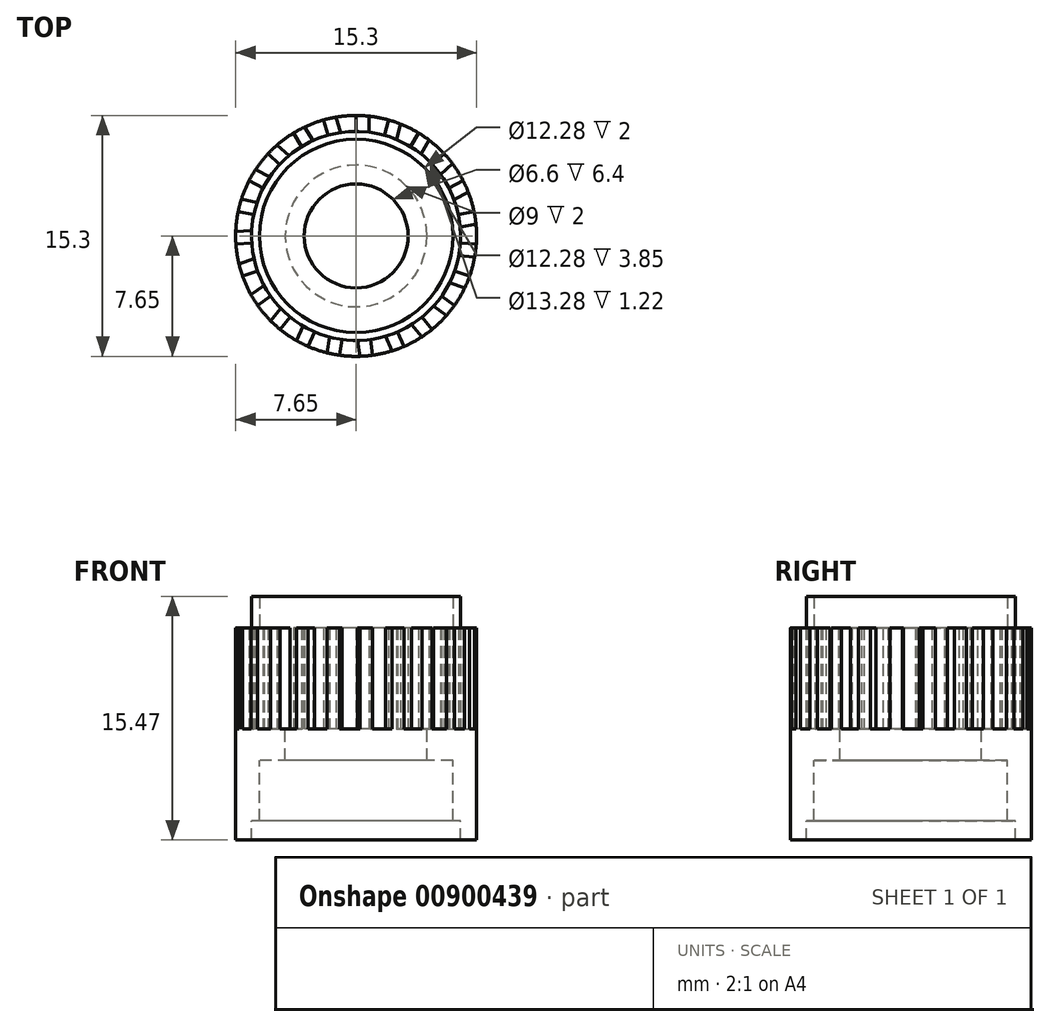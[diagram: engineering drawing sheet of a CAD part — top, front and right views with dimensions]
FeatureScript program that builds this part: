
annotation { "Feature Type Name" : "Feature", "Feature Type Description" : "" }
export const myFeature = defineFeature(function(context is Context, id is Id, definition is map)
    precondition{}
    {
        {
            var Q0;
            Q0=qCreatedBy(makeId("Top.planeOp"),FACE);
            var sketch = newSketch(context, id + "F0", { "sketchPlane" : qUnion([Q0])});
            skCircle(sketch, "E0", {"center": v(0, 0.97) * mm, "radius": 6.14 * mm});
            skCircle(sketch, "E1", {"center": v(0, 0.97) * mm, "radius": 7.65 * mm});
            skLineSegment(sketch, "E2", {"start": v(0, 7.11) * mm, "end": v(0, 8.62) * mm});
            skLineSegment(sketch, "E3", {"start": v(0.8, 7.06) * mm, "end": v(0.8, 8.58) * mm});
            skCircle(sketch, "E4", {"center": v(0, 0.97) * mm, "radius": 3.3 * mm});
            skCircle(sketch, "E5", {"center": v(0, 0.97) * mm, "radius": 4.5 * mm});
            skCircle(sketch, "E6", {"center": v(0, 0.97) * mm, "radius": 6.64 * mm});
            skCircle(sketch, "E7", {"center": v(0, 0.97) * mm, "radius": 7.45 * mm});
            skCircle(sketch, "E8", {"center": v(0, 0.97) * mm, "radius": 9 * mm});
            skCircle(sketch, "E9", {"center": v(0, 0.97) * mm, "radius": 10 * mm});
            skSolve(sketch);
        }
        {
            var Q0;
            Q0=makeQuery(id+"F0.imprint","IMPRINT",FACE,{"disambiguationData":[TD([[makeQuery(id+"F0.imprint","IMPRINT",EDGE,{"derivedFrom":sQuery(id+"F0.wireOp",EDGE,"E4")}),-1.0]])]});
            var Q1;
            Q1=makeQuery(id+"F0.imprint","IMPRINT",FACE,{"disambiguationData":[TD([[makeQuery(id+"F0.imprint","IMPRINT",EDGE,{"derivedFrom":sQuery(id+"F0.wireOp",EDGE,"E5")}),-1.0]])]});
            var Q2;
            {var subQ0=sQuery(id+"F0.wireOp",EDGE,"E2");var subQ1=sQuery(id+"F0.wireOp",EDGE,"E0");var subQ2=makeQuery(id+"F0.imprint","INTERSECT",VERTEX,{"derivedFrom":[subQ1,subQ0]});Q2=makeQuery(id+"F0.imprint","IMPRINT",FACE,{"disambiguationData":[TD([[makeQuery(id+"F0.imprint","IMPRINT",EDGE,{"disambiguationData":[TD([[subQ2,1.0]])],"derivedFrom":subQ1}),-1.0]])]});}
            var Q3;
            {var subQ0=sQuery(id+"F0.wireOp",EDGE,"E6");var subQ1=sQuery(id+"F0.wireOp",EDGE,"E2");var subQ2=makeQuery(id+"F0.imprint","INTERSECT",VERTEX,{"derivedFrom":[subQ1,subQ0]});Q3=makeQuery(id+"F0.imprint","IMPRINT",FACE,{"disambiguationData":[TD([[makeQuery(id+"F0.imprint","IMPRINT",EDGE,{"disambiguationData":[TD([[subQ2,-1.0]])],"derivedFrom":subQ1}),-1.0]])]});}
            var Q4;
            {var subQ0=sQuery(id+"F0.wireOp",EDGE,"E2");var subQ1=sQuery(id+"F0.wireOp",EDGE,"E1");var subQ2=makeQuery(id+"F0.imprint","INTERSECT",VERTEX,{"derivedFrom":[subQ1,subQ0]});Q4=makeQuery(id+"F0.imprint","IMPRINT",FACE,{"disambiguationData":[TD([[makeQuery(id+"F0.imprint","IMPRINT",EDGE,{"disambiguationData":[TD([[subQ2,1.0]])],"derivedFrom":subQ1}),1.0]])]});}
            extrude(context, id + "F1", {"entities" : qUnion([Q0, Q1, Q2, Q3, Q4]), "depth" : 6.4 * mm, "offsetDistance" : 25 * mm});
        }
        {
            var Q0;
            {var subQ0=sQuery(id+"F0.wireOp",EDGE,"E2");var subQ1=sQuery(id+"F0.wireOp",EDGE,"E0");var subQ2=makeQuery(id+"F0.imprint","INTERSECT",VERTEX,{"derivedFrom":[subQ1,subQ0]});Q0=makeQuery(id+"F0.imprint","IMPRINT",FACE,{"disambiguationData":[TD([[makeQuery(id+"F0.imprint","IMPRINT",EDGE,{"disambiguationData":[TD([[subQ2,-1.0]])],"derivedFrom":subQ1}),-1.0]])]});}
            var Q1;
            {var subQ0=sQuery(id+"F0.wireOp",EDGE,"E2");var subQ1=sQuery(id+"F0.wireOp",EDGE,"E0");var subQ2=makeQuery(id+"F0.imprint","INTERSECT",VERTEX,{"derivedFrom":[subQ1,subQ0]});Q1=makeQuery(id+"F0.imprint","IMPRINT",FACE,{"disambiguationData":[TD([[makeQuery(id+"F0.imprint","IMPRINT",EDGE,{"disambiguationData":[TD([[subQ2,1.0]])],"derivedFrom":subQ1}),-1.0]])]});}
            extrude(context, id + "F2", {"entities" : qUnion([Q0, Q1]), "depth" : 8.4 * mm, "offsetDistance" : 25 * mm});
        }
        {
            var Q0;
            Q0=qCreatedBy(makeId("Right.planeOp"),FACE);
            var sketch = newSketch(context, id + "F3", { "sketchPlane" : qUnion([Q0])});
            skLineSegment(sketch, "E10", {"start": v(0.97, 0) * mm, "end": v(0.97, -2.16) * mm});
            skSolve(sketch);
        }
        {
            var Q0;
            Q0=makeQuery(id+"F1.opExtrude","SWEPT_BODY",BODY,{"disambiguationData":[OSD([sQuery(id+"F0.wireOp",EDGE,"E0"),sQuery(id+"F0.wireOp",EDGE,"E1"),sQuery(id+"F0.wireOp",EDGE,"E2"),sQuery(id+"F0.wireOp",EDGE,"E3"),sQuery(id+"F0.wireOp",EDGE,"E4")])]});
            var Q1;
            Q1=sQuery(id+"F3.wireOp",EDGE,"E10");
            circularPattern(context, id + "F4", {"operationType" : NewBodyOperationType.ADD, "entities" : qUnion([Q0]), "axis" : qUnion([Q1]), "angle" : 360 * degree, "instanceCount" : 23, "equalSpace" : true});
        }
        {
            var Q0;
            Q0=makeQuery(id+"F0.imprint","IMPRINT",FACE,{"disambiguationData":[TD([[makeQuery(id+"F0.imprint","IMPRINT",EDGE,{"derivedFrom":sQuery(id+"F0.wireOp",EDGE,"E5")}),-1.0]])]});
            extrude(context, id + "F5", {"entities" : qUnion([Q0]), "operationType" : NewBodyOperationType.ADD, "oppositeDirection" : true, "depth" : 2 * mm, "offsetDistance" : 25 * mm});
        }
        {
            var Q0;
            {var subQ0=sQuery(id+"F0.wireOp",EDGE,"E2");var subQ1=sQuery(id+"F0.wireOp",EDGE,"E0");var subQ2=makeQuery(id+"F0.imprint","INTERSECT",VERTEX,{"derivedFrom":[subQ1,subQ0]});Q0=makeQuery(id+"F0.imprint","IMPRINT",FACE,{"disambiguationData":[TD([[makeQuery(id+"F0.imprint","IMPRINT",EDGE,{"disambiguationData":[TD([[subQ2,-1.0]])],"derivedFrom":subQ1}),-1.0]])]});}
            var Q1;
            {var subQ0=sQuery(id+"F0.wireOp",EDGE,"E2");var subQ1=sQuery(id+"F0.wireOp",EDGE,"E0");var subQ2=makeQuery(id+"F0.imprint","INTERSECT",VERTEX,{"derivedFrom":[subQ1,subQ0]});Q1=makeQuery(id+"F0.imprint","IMPRINT",FACE,{"disambiguationData":[TD([[makeQuery(id+"F0.imprint","IMPRINT",EDGE,{"disambiguationData":[TD([[subQ2,1.0]])],"derivedFrom":subQ1}),-1.0]])]});}
            extrude(context, id + "F6", {"entities" : qUnion([Q0, Q1]), "operationType" : NewBodyOperationType.ADD, "oppositeDirection" : true, "depth" : 5.85 * mm, "offsetDistance" : 25 * mm});
        }
        {
            var Q0;
            {var subQ0=sQuery(id+"F0.wireOp",EDGE,"E6");var subQ1=sQuery(id+"F0.wireOp",EDGE,"E2");var subQ2=makeQuery(id+"F0.imprint","INTERSECT",VERTEX,{"derivedFrom":[subQ1,subQ0]});Q0=makeQuery(id+"F0.imprint","IMPRINT",FACE,{"disambiguationData":[TD([[makeQuery(id+"F0.imprint","IMPRINT",EDGE,{"disambiguationData":[TD([[subQ2,-1.0]])],"derivedFrom":subQ1}),1.0]])]});}
            var Q1;
            {var subQ0=sQuery(id+"F0.wireOp",EDGE,"E2");var subQ1=sQuery(id+"F0.wireOp",EDGE,"E1");var subQ2=makeQuery(id+"F0.imprint","INTERSECT",VERTEX,{"derivedFrom":[subQ1,subQ0]});Q1=makeQuery(id+"F0.imprint","IMPRINT",FACE,{"disambiguationData":[TD([[makeQuery(id+"F0.imprint","IMPRINT",EDGE,{"disambiguationData":[TD([[subQ2,-1.0]])],"derivedFrom":subQ1}),1.0]])]});}
            var Q2;
            {var subQ0=sQuery(id+"F0.wireOp",EDGE,"E6");var subQ1=sQuery(id+"F0.wireOp",EDGE,"E2");var subQ2=makeQuery(id+"F0.imprint","INTERSECT",VERTEX,{"derivedFrom":[subQ1,subQ0]});Q2=makeQuery(id+"F0.imprint","IMPRINT",FACE,{"disambiguationData":[TD([[makeQuery(id+"F0.imprint","IMPRINT",EDGE,{"disambiguationData":[TD([[subQ2,-1.0]])],"derivedFrom":subQ1}),-1.0]])]});}
            var Q3;
            {var subQ0=sQuery(id+"F0.wireOp",EDGE,"E2");var subQ1=sQuery(id+"F0.wireOp",EDGE,"E1");var subQ2=makeQuery(id+"F0.imprint","INTERSECT",VERTEX,{"derivedFrom":[subQ1,subQ0]});Q3=makeQuery(id+"F0.imprint","IMPRINT",FACE,{"disambiguationData":[TD([[makeQuery(id+"F0.imprint","IMPRINT",EDGE,{"disambiguationData":[TD([[subQ2,1.0]])],"derivedFrom":subQ1}),1.0]])]});}
            extrude(context, id + "F7", {"entities" : qUnion([Q0, Q1, Q2, Q3]), "operationType" : NewBodyOperationType.ADD, "oppositeDirection" : true, "depth" : 7.07 * mm, "offsetDistance" : 25 * mm});
        }
    });
